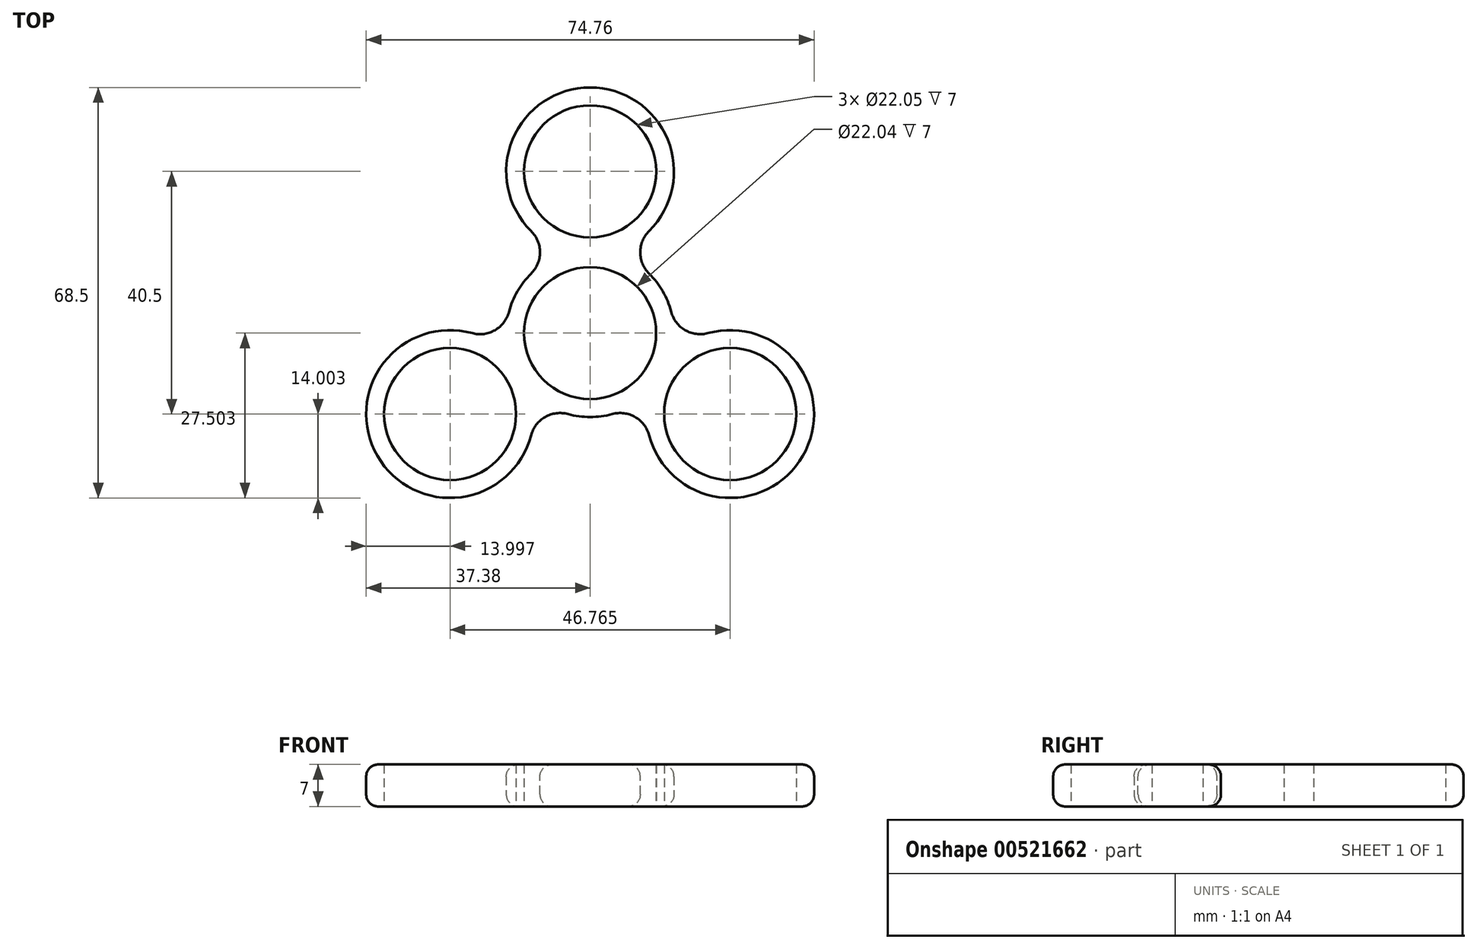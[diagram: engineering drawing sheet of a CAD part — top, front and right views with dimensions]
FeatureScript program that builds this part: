
annotation { "Feature Type Name" : "Feature", "Feature Type Description" : "" }
export const myFeature = defineFeature(function(context is Context, id is Id, definition is map)
    precondition{}
    {
        {
            var Q0;
            Q0=qCreatedBy(makeId("Top.planeOp"),FACE);
            var sketch = newSketch(context, id + "F0", { "sketchPlane" : qUnion([Q0])});
            skCircle(sketch, "E0", {"center": v(0, 23.74) * mm, "radius": 11.03 * mm});
            skCircle(sketch, "E1.1.0", {"center": v(-23.38, -16.76) * mm, "radius": 11.03 * mm});
            skCircle(sketch, "E1.2.0", {"center": v(23.38, -16.76) * mm, "radius": 11.03 * mm});
            skPoint(sketch, "E1.center", {"position": v(0, -3.26) * mm});
            skArc(sketch, "E2", {"start": v(3.7, 10.24) * mm, "mid": v(0, 37.74) * mm, "end": v(-3.7, 10.24) * mm});
            skArc(sketch, "E3.1.0", {"start": v(-13.55, -6.8) * mm, "mid": v(-35.5, -23.76) * mm, "end": v(-9.84, -13.22) * mm});
            skArc(sketch, "E3.2.0", {"start": v(9.84, -13.22) * mm, "mid": v(35.5, -23.76) * mm, "end": v(13.55, -6.8) * mm});
            skCircle(sketch, "E4", {"center": v(0, -3.26) * mm, "radius": 11.02 * mm});
            skArc(sketch, "E5", {"start": v(-3.7, 10.24) * mm, "mid": v(-12.12, 3.74) * mm, "end": v(-13.55, -6.8) * mm});
            skPoint(sketch, "E6", {"position": v(0, 37.74) * mm});
            skArc(sketch, "E7.trimOffspring", {"start": v(13.55, -6.8) * mm, "mid": v(12.12, 3.74) * mm, "end": v(3.7, 10.24) * mm});
            skArc(sketch, "E8.trimOffspring", {"start": v(-9.84, -13.22) * mm, "mid": v(0, -17.26) * mm, "end": v(9.84, -13.22) * mm});
            skSolve(sketch);
        }
        {
            var Q0;
            Q0=makeQuery(id+"F0.imprint","IMPRINT",FACE,{"disambiguationData":[TD([[makeQuery(id+"F0.imprint","IMPRINT",EDGE,{"derivedFrom":sQuery(id+"F0.wireOp",EDGE,"E1.2.0")}),-1.0]])]});
            var Q1;
            Q1=makeQuery(id+"F0.imprint","IMPRINT",FACE,{"disambiguationData":[TD([[makeQuery(id+"F0.imprint","IMPRINT",EDGE,{"derivedFrom":sQuery(id+"F0.wireOp",EDGE,"E4")}),-1.0]])]});
            var Q2;
            Q2=makeQuery(id+"F0.imprint","IMPRINT",FACE,{"disambiguationData":[TD([[makeQuery(id+"F0.imprint","IMPRINT",EDGE,{"derivedFrom":sQuery(id+"F0.wireOp",EDGE,"E0")}),-1.0]])]});
            var Q3;
            Q3=makeQuery(id+"F0.imprint","IMPRINT",FACE,{"disambiguationData":[TD([[makeQuery(id+"F0.imprint","IMPRINT",EDGE,{"derivedFrom":sQuery(id+"F0.wireOp",EDGE,"E1.1.0")}),-1.0]])]});
            extrude(context, id + "F1", {"entities" : qUnion([Q0, Q1, Q2, Q3]), "depth" : 7 * mm, "offsetDistance" : 25 * mm});
        }
        {
            var Q0;
            Q0=makeQuery(id+"F1.opExtrude","SWEPT_EDGE",EDGE,{"disambiguationData":[OSD([sQuery(id+"F0.wireOp",EDGE,"E3.1.0"),sQuery(id+"F0.wireOp",EDGE,"E5")])]});
            var Q1;
            Q1=makeQuery(id+"F1.opExtrude","SWEPT_EDGE",EDGE,{"disambiguationData":[OSD([sQuery(id+"F0.wireOp",EDGE,"E3.1.0"),sQuery(id+"F0.wireOp",EDGE,"E8.trimOffspring")])]});
            var Q2;
            Q2=makeQuery(id+"F1.opExtrude","SWEPT_EDGE",EDGE,{"disambiguationData":[OSD([sQuery(id+"F0.wireOp",EDGE,"E3.2.0"),sQuery(id+"F0.wireOp",EDGE,"E8.trimOffspring")])]});
            var Q3;
            Q3=makeQuery(id+"F1.opExtrude","SWEPT_EDGE",EDGE,{"disambiguationData":[OSD([sQuery(id+"F0.wireOp",EDGE,"E3.2.0"),sQuery(id+"F0.wireOp",EDGE,"E7.trimOffspring")])]});
            var Q4;
            Q4=makeQuery(id+"F1.opExtrude","SWEPT_EDGE",EDGE,{"disambiguationData":[OSD([sQuery(id+"F0.wireOp",EDGE,"E2"),sQuery(id+"F0.wireOp",EDGE,"E7.trimOffspring")])]});
            var Q5;
            Q5=makeQuery(id+"F1.opExtrude","SWEPT_EDGE",EDGE,{"disambiguationData":[OSD([sQuery(id+"F0.wireOp",EDGE,"E2"),sQuery(id+"F0.wireOp",EDGE,"E5")])]});
            fillet(context, id + "F2", {"entities" : qUnion([Q0, Q1, Q2, Q3, Q4, Q5]), "radius" : 5 * mm, "tangentPropagation" : true, "allowEdgeOverflow" : false});
        }
        {
            var Q0;
            Q0=makeQuery(id+"F1.opExtrude","CAP_EDGE",EDGE,{"disambiguationData":[OSD([sQuery(id+"F0.wireOp",EDGE,"E2")])],"isStart":false});
            var Q1;
            Q1=makeQuery(id+"F1.opExtrude","CAP_EDGE",EDGE,{"disambiguationData":[OSD([sQuery(id+"F0.wireOp",EDGE,"E3.1.0")])],"isStart":true});
            fillet(context, id + "F3", {"entities" : qUnion([Q0, Q1]), "radius" : 2 * mm, "tangentPropagation" : true, "allowEdgeOverflow" : false});
        }
    });
